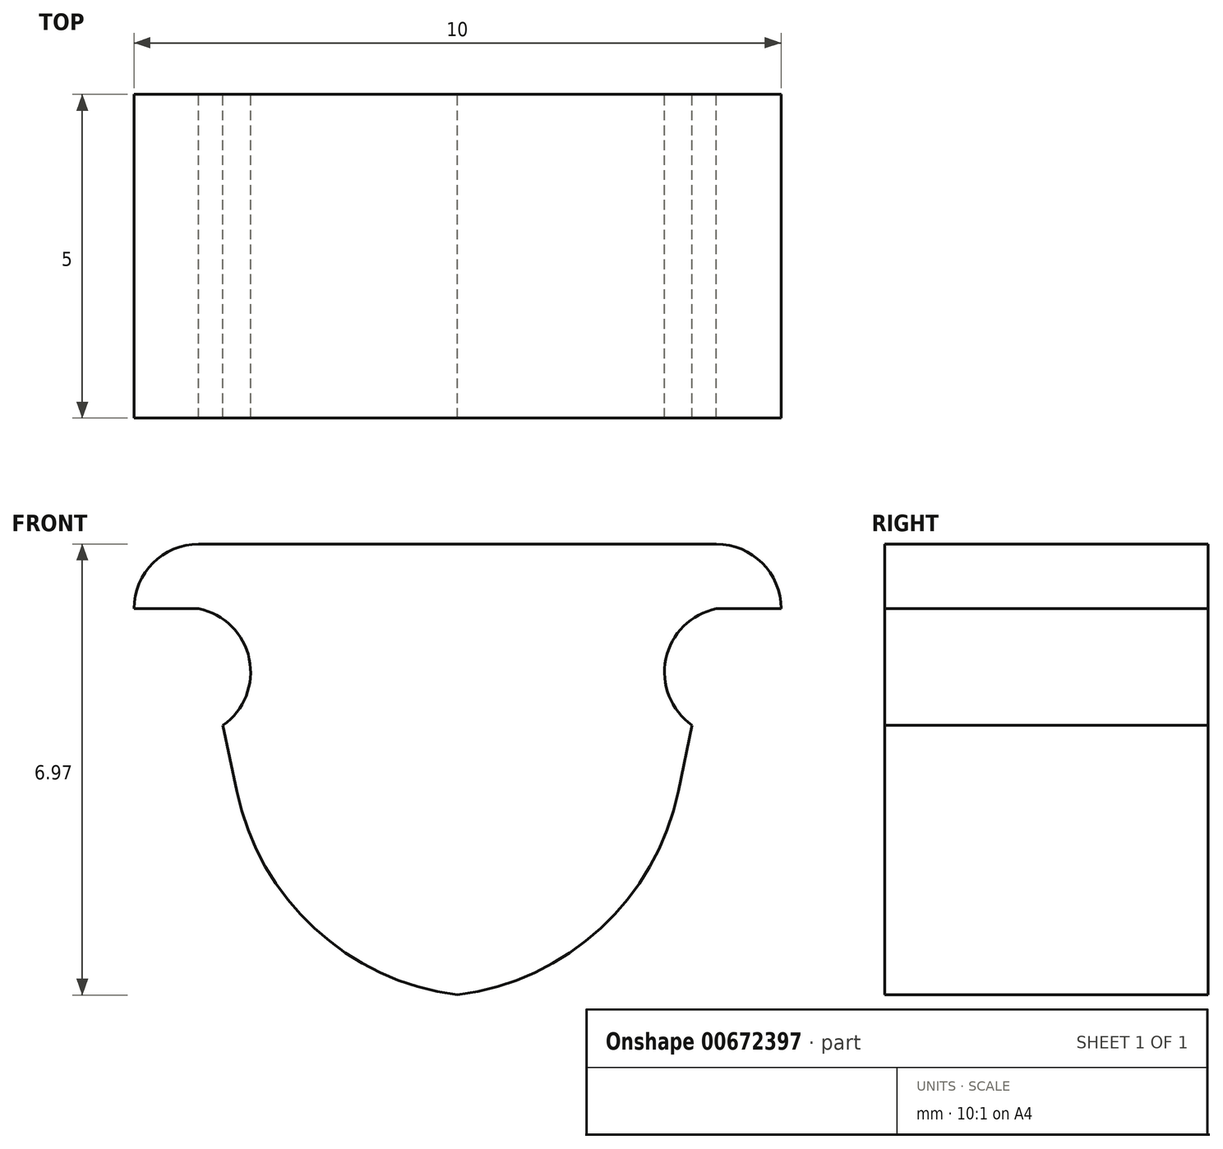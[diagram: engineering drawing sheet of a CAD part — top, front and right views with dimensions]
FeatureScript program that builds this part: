
annotation { "Feature Type Name" : "Feature", "Feature Type Description" : "" }
export const myFeature = defineFeature(function(context is Context, id is Id, definition is map)
    precondition{}
    {
        {
            var Q0;
            Q0=qCreatedBy(makeId("Front.planeOp"),FACE);
            var sketch = newSketch(context, id + "F0", { "sketchPlane" : qUnion([Q0])});
            skLineSegment(sketch, "E0.bottom", {"start": v(5, -0.5) * mm, "end": v(4, -0.5) * mm});
            skLineSegment(sketch, "E0.top", {"start": v(4, 0.5) * mm, "end": v(-4, 0.5) * mm});
            skLineSegment(sketch, "E0.left", {"start": v(5, -0.5) * mm, "end": v(5, -0.5) * mm});
            skLineSegment(sketch, "E0.right", {"start": v(-5, -0.5) * mm, "end": v(-5, -0.5) * mm});
            skPoint(sketch, "E0.middle", {"position": v(0, 0) * mm});
            skLineSegment(sketch, "E1", {"start": v(0, 0) * mm, "end": v(0, -6.5) * mm, "construction": true});
            skLineSegment(sketch, "E2", {"start": v(-3.62, -2.3) * mm, "end": v(-2.75, -6.5) * mm});
            skLineSegment(sketch, "E3", {"start": v(-2.75, -6.5) * mm, "end": v(0, -6.5) * mm});
            skLineSegment(sketch, "E4.MirrorCS", {"start": v(2.75, -6.5) * mm, "end": v(0, -6.5) * mm});
            skArc(sketch, "E5", {"start": v(-3.62, -2.3) * mm, "mid": v(-3.22, -1.28) * mm, "end": v(-4, -0.5) * mm});
            skPoint(sketch, "E6.MirrorCS.end.orphan", {"position": v(2.75, -6.5) * mm});
            skPoint(sketch, "E6.MirrorCS.start.orphan", {"position": v(4, -0.5) * mm});
            skLineSegment(sketch, "E7.MirrorCS", {"start": v(3.62, -2.3) * mm, "end": v(2.75, -6.5) * mm});
            skArc(sketch, "E8.MirrorCS", {"start": v(3.62, -2.3) * mm, "mid": v(3.22, -1.28) * mm, "end": v(4, -0.5) * mm});
            skLineSegment(sketch, "E9.trimOffspring", {"start": v(-4, -0.5) * mm, "end": v(-5, -0.5) * mm});
            skPoint(sketch, "E10.visualSharp", {"position": v(-5, 0.5) * mm});
            skArc(sketch, "E10.filletArc", {"start": v(-4, 0.5) * mm, "mid": v(-4.7, 0.2) * mm, "end": v(-5, -0.5) * mm});
            skPoint(sketch, "E11.visualSharp", {"position": v(5, 0.5) * mm});
            skArc(sketch, "E11.filletArc", {"start": v(5, -0.5) * mm, "mid": v(4.7, 0.2) * mm, "end": v(4, 0.5) * mm});
            skSolve(sketch);
        }
        {
            var Q0;
            Q0=makeQuery(id+"F0.imprint","IMPRINT",FACE,{"disambiguationData":[TD([[makeQuery(id+"F0.imprint","IMPRINT",EDGE,{"derivedFrom":sQuery(id+"F0.wireOp",EDGE,"E0.bottom")}),-1.0]])]});
            extrude(context, id + "F1", {"entities" : qUnion([Q0]), "depth" : 5 * mm, "offsetDistance" : 25 * mm});
        }
        {
            var Q0;
            Q0=makeQuery(id+"F1.opExtrude","SWEPT_EDGE",EDGE,{"disambiguationData":[OSD([sQuery(id+"F0.wireOp",EDGE,"E2"),sQuery(id+"F0.wireOp",EDGE,"E3")])]});
            var Q1;
            Q1=makeQuery(id+"F1.opExtrude","SWEPT_EDGE",EDGE,{"disambiguationData":[OSD([sQuery(id+"F0.wireOp",EDGE,"E4.MirrorCS"),sQuery(id+"F0.wireOp",EDGE,"E7.MirrorCS")])]});
            fillet(context, id + "F2", {"entities" : qUnion([Q0, Q1]), "radius" : 4 * mm, "tangentPropagation" : true, "allowEdgeOverflow" : false});
        }
    });
